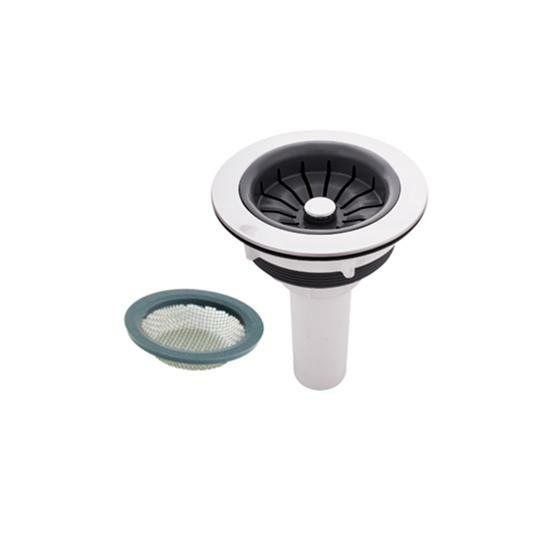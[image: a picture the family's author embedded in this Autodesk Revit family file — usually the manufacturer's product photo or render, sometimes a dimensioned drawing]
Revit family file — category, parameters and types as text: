
# Revit family: 01-31706-11 LAVAPLATOS EN ACERO POCETA 43 CM DE DIÁMETRO
name_source: partatom
category: Aparatos sanitarios
revit_build: Autodesk Revit 2018 (Build: 20170223_1515(x64)
units: mm (PartAtom-declared; Revit-internal decimal feet)

## family parameters
Anfitrión = Cara
Compartido = No
Corte con vacíos al cargar = No
Cota de conector redondo = Diámetro de uso
Número OmniClass = 23.31.11.00
Punto de cálculo de habitación = No
Tipo de pieza = Normal

## types (1)
- 01-31706-11
    Acero inox = Acero inoxidable
    Alto = 180 mm
    Ancho = 430 mm
    Conexión AC = Sí
    Conexión AF = Sí
    Conexión de residuos = No
    Conexión de ventilación = No
    Descripción = Lavaplatos en acero
    Elevación por defecto = 0 mm  [stored 0 ft]
    Fabricante = Gricol
    Imagen de tipo = <Ninguno>
    Largo = 420 mm
    Link Ficha Tecnica = No existe
    Modelo = 01-31706-11
    Product Name = LAVAPLATOS EN ACERO POCETA 43 CM DE DIÁMETRO
    URL = https://www.gricol.com

note: [stored X ft] marks values corroborated as IEEE doubles in the binary element streams (Revit-internal decimal feet)

## geometry (parser evidence)
native form markers: Blend x4, Sweep x13
no freeform markers — native parametric forms only
